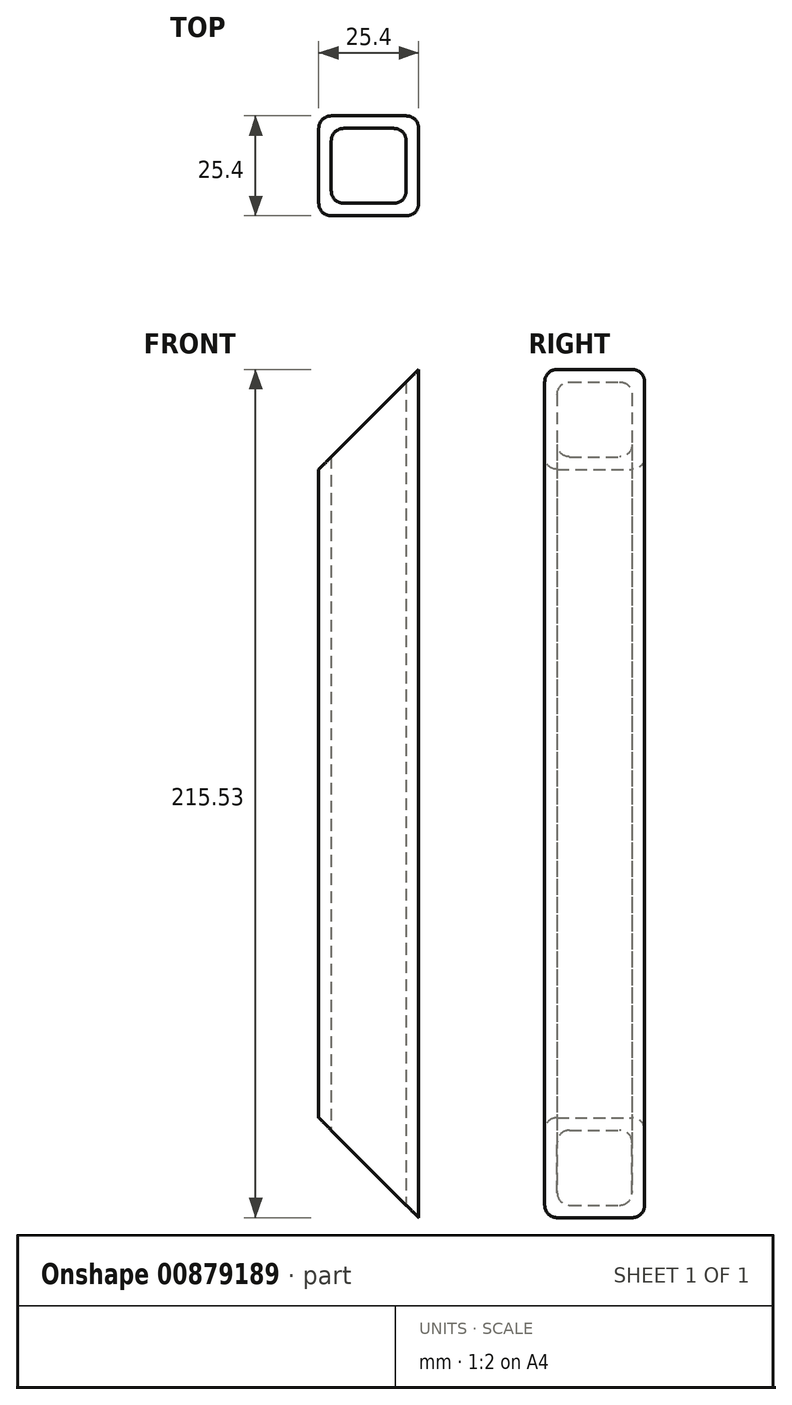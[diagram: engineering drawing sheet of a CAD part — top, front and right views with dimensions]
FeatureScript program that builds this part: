
annotation { "Feature Type Name" : "Feature", "Feature Type Description" : "" }
export const myFeature = defineFeature(function(context is Context, id is Id, definition is map)
    precondition{}
    {
        {
            var Q0;
            Q0=qCreatedBy(makeId("Top.planeOp"),FACE);
            var sketch = newSketch(context, id + "F0", { "sketchPlane" : qUnion([Q0])});
            skLineSegment(sketch, "E0.bottom", {"start": v(8.79, -11.72) * mm, "end": v(-10.26, -11.72) * mm});
            skLineSegment(sketch, "E0.top", {"start": v(8.79, 13.68) * mm, "end": v(-10.26, 13.68) * mm});
            skLineSegment(sketch, "E0.left", {"start": v(11.96, -8.55) * mm, "end": v(11.96, 10.5) * mm});
            skLineSegment(sketch, "E0.right", {"start": v(-13.44, -8.55) * mm, "end": v(-13.44, 10.5) * mm});
            skLineSegment(sketch, "E1.bottom", {"start": v(5.61, -8.55) * mm, "end": v(-7.09, -8.55) * mm});
            skLineSegment(sketch, "E1.top", {"start": v(5.61, 10.5) * mm, "end": v(-7.09, 10.5) * mm});
            skLineSegment(sketch, "E1.left", {"start": v(8.79, -5.37) * mm, "end": v(8.79, 7.33) * mm});
            skLineSegment(sketch, "E1.right", {"start": v(-10.26, -5.37) * mm, "end": v(-10.26, 7.33) * mm});
            skPoint(sketch, "E2.visualSharp", {"position": v(8.79, 10.5) * mm});
            skArc(sketch, "E2.filletArc", {"start": v(8.79, 7.33) * mm, "mid": v(7.86, 9.57) * mm, "end": v(5.61, 10.5) * mm});
            skPoint(sketch, "E3.visualSharp", {"position": v(-10.26, 10.5) * mm});
            skArc(sketch, "E3.filletArc", {"start": v(-7.09, 10.5) * mm, "mid": v(-9.34, 9.57) * mm, "end": v(-10.26, 7.33) * mm});
            skPoint(sketch, "E4.visualSharp", {"position": v(-10.26, -8.55) * mm});
            skArc(sketch, "E4.filletArc", {"start": v(-10.26, -5.37) * mm, "mid": v(-9.34, -7.62) * mm, "end": v(-7.09, -8.55) * mm});
            skPoint(sketch, "E5.visualSharp", {"position": v(8.79, -8.55) * mm});
            skArc(sketch, "E5.filletArc", {"start": v(5.61, -8.55) * mm, "mid": v(7.86, -7.62) * mm, "end": v(8.79, -5.37) * mm});
            skPoint(sketch, "E6.visualSharp", {"position": v(11.96, 13.68) * mm});
            skArc(sketch, "E6.filletArc", {"start": v(11.96, 10.5) * mm, "mid": v(11.03, 12.75) * mm, "end": v(8.79, 13.68) * mm});
            skPoint(sketch, "E7.visualSharp", {"position": v(-13.44, 13.68) * mm});
            skArc(sketch, "E7.filletArc", {"start": v(-10.26, 13.68) * mm, "mid": v(-12.51, 12.75) * mm, "end": v(-13.44, 10.5) * mm});
            skPoint(sketch, "E8.visualSharp", {"position": v(-13.44, -11.72) * mm});
            skArc(sketch, "E8.filletArc", {"start": v(-13.44, -8.55) * mm, "mid": v(-12.51, -10.8) * mm, "end": v(-10.26, -11.72) * mm});
            skPoint(sketch, "E9.visualSharp", {"position": v(11.96, -11.72) * mm});
            skArc(sketch, "E9.filletArc", {"start": v(8.79, -11.72) * mm, "mid": v(11.03, -10.8) * mm, "end": v(11.96, -8.55) * mm});
            skSolve(sketch);
        }
        {
            var Q0;
            Q0=qSketchRegion(id+"F0",true);
            extrude(context, id + "F1", {"entities" : qUnion([Q0]), "depth" : 215.53 * mm, "offsetDistance" : 25.4 * mm});
        }
        {
            var Q0;
            Q0=qCreatedBy(makeId("Front.planeOp"),FACE);
            var sketch = newSketch(context, id + "F2", { "sketchPlane" : qUnion([Q0])});
            skLineSegment(sketch, "E10.bottom", {"start": v(11.96, 0) * mm, "end": v(-13.44, 0) * mm});
            skLineSegment(sketch, "E10.top", {"start": v(11.96, 25.4) * mm, "end": v(-13.44, 25.4) * mm});
            skLineSegment(sketch, "E10.left", {"start": v(11.96, 0) * mm, "end": v(11.96, 25.4) * mm});
            skLineSegment(sketch, "E10.right", {"start": v(-13.44, 0) * mm, "end": v(-13.44, 25.4) * mm});
            skLineSegment(sketch, "E11", {"start": v(-13.44, 25.4) * mm, "end": v(11.96, 0) * mm});
            skSolve(sketch);
        }
        {
            var Q0;
            Q0=qCreatedBy(makeId("Front.planeOp"),FACE);
            var sketch = newSketch(context, id + "F3", { "sketchPlane" : qUnion([Q0])});
            skLineSegment(sketch, "E12.bottom", {"start": v(11.96, 190.13) * mm, "end": v(-13.44, 190.13) * mm});
            skLineSegment(sketch, "E12.top", {"start": v(11.96, 215.53) * mm, "end": v(-13.44, 215.53) * mm});
            skLineSegment(sketch, "E12.left", {"start": v(11.96, 190.13) * mm, "end": v(11.96, 215.53) * mm});
            skLineSegment(sketch, "E12.right", {"start": v(-13.44, 190.13) * mm, "end": v(-13.44, 215.53) * mm});
            skLineSegment(sketch, "E13", {"start": v(-13.44, 190.13) * mm, "end": v(11.96, 215.53) * mm});
            skSolve(sketch);
        }
        {
            var Q0;
            Q0=makeQuery(id+"F2.imprint","IMPRINT",FACE,{"disambiguationData":[TD([[makeQuery(id+"F2.imprint","IMPRINT",EDGE,{"derivedFrom":sQuery(id+"F2.wireOp",EDGE,"E10.bottom")}),-1.0]])]});
            extrude(context, id + "F4", {"entities" : qUnion([Q0]), "operationType" : NewBodyOperationType.REMOVE, "endBound" : BoundingType.SYMMETRIC, "depth" : 50.8 * mm, "offsetDistance" : 25.4 * mm});
        }
        {
            var Q0;
            Q0=makeQuery(id+"F3.imprint","IMPRINT",FACE,{"disambiguationData":[TD([[makeQuery(id+"F3.imprint","IMPRINT",EDGE,{"derivedFrom":sQuery(id+"F3.wireOp",EDGE,"E12.top")}),1.0]])]});
            extrude(context, id + "F5", {"entities" : qUnion([Q0]), "operationType" : NewBodyOperationType.REMOVE, "endBound" : BoundingType.SYMMETRIC, "depth" : 50.8 * mm, "offsetDistance" : 25.4 * mm});
        }
    });
